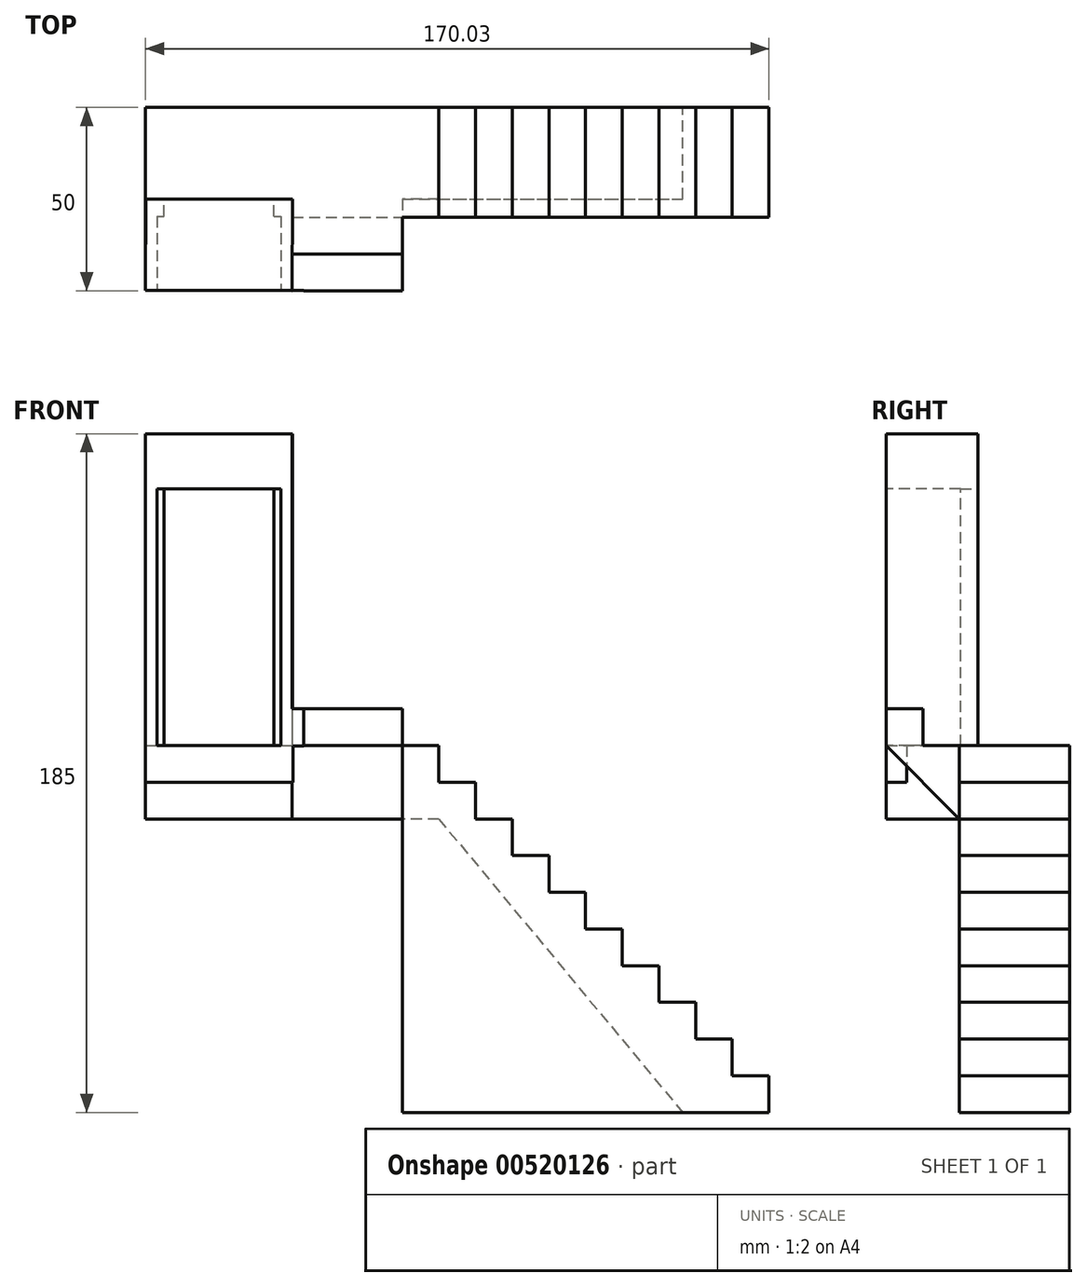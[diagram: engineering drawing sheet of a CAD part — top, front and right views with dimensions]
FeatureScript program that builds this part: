
annotation { "Feature Type Name" : "Feature", "Feature Type Description" : "" }
export const myFeature = defineFeature(function(context is Context, id is Id, definition is map)
    precondition{}
    {
        {
            var Q0;
            Q0=qCreatedBy(makeId("Top.planeOp"),FACE);
            var sketch = newSketch(context, id + "F0", { "sketchPlane" : qUnion([Q0])});
            skLineSegment(sketch, "E0.bottom", {"start": v(-73.69, 46.23) * mm, "end": v(106.31, 46.23) * mm});
            skLineSegment(sketch, "E0.top", {"start": v(-33.69, 16.23) * mm, "end": v(106.31, 16.23) * mm});
            skLineSegment(sketch, "E0.left", {"start": v(-73.69, 46.23) * mm, "end": v(-73.69, 16.23) * mm});
            skLineSegment(sketch, "E0.right", {"start": v(106.31, 46.23) * mm, "end": v(106.31, 16.23) * mm});
            skLineSegment(sketch, "E1", {"start": v(-3.69, 16.23) * mm, "end": v(-3.69, -3.77) * mm});
            skLineSegment(sketch, "E2", {"start": v(-3.69, -3.77) * mm, "end": v(-33.69, -3.77) * mm});
            skLineSegment(sketch, "E3", {"start": v(-33.69, -3.77) * mm, "end": v(-33.69, 16.23) * mm});
            skLineSegment(sketch, "E4", {"start": v(-33.69, 16.23) * mm, "end": v(-33.69, 46.23) * mm});
            skLineSegment(sketch, "E5", {"start": v(-73.69, 16.23) * mm, "end": v(-73.69, -3.71) * mm});
            skLineSegment(sketch, "E6", {"start": v(-73.69, -3.71) * mm, "end": v(-33.69, -3.77) * mm});
            skSolve(sketch);
        }
        {
            var Q0;
            Q0 = qSketchRegion(id + "F0", true);
            extrude(context, id + "F1", {"entities" : qUnion([Q0]), "depth" : 100 * mm, "offsetDistance" : 25 * mm});
        }
        {
            var Q0;
            Q0=makeQuery(id+"F1.opExtrude","SWEPT_FACE",FACE,{"disambiguationData":[OSD([sQuery(id+"F0.wireOp",EDGE,"E0.bottom")])]});
            var sketch = newSketch(context, id + "F2", { "sketchPlane" : qUnion([Q0])});
            skLineSegment(sketch, "E7", {"start": v(-6.31, 100) * mm, "end": v(-6.31, 0) * mm, "construction": true});
            skLineSegment(sketch, "E8", {"start": v(-106.31, 0) * mm, "end": v(-6.31, 100) * mm});
            skLineSegment(sketch, "E9", {"start": v(-6.31, 100) * mm, "end": v(-6.31, 80) * mm});
            skLineSegment(sketch, "E10", {"start": v(-6.31, 80) * mm, "end": v(73.69, 80) * mm});
            skLineSegment(sketch, "E11", {"start": v(-6.31, 80) * mm, "end": v(-6.31, 0) * mm});
            skSolve(sketch);
        }
        {
            var Q0;
            Q0 = qSketchRegion(id + "F2", true);
            var Q1;
            {var subQ0=sQuery(id+"F2.wireOp",EDGE,"E8");Q1=makeQuery(id+"F2.imprint","IMPRINT",FACE,{"disambiguationData":[TD([[makeQuery(id+"F2.imprint","IMPRINT",EDGE,{"derivedFrom":subQ0}),1.0]])]});}
            var Q2;
            {var subQ0=sQuery(id+"F2.wireOp",EDGE,"E10");Q2=makeQuery(id+"F2.imprint","IMPRINT",FACE,{"disambiguationData":[TD([[makeQuery(id+"F2.imprint","IMPRINT",EDGE,{"derivedFrom":subQ0}),-1.0]])]});}
            extrude(context, id + "F3", {"entities" : qUnion([Q0, Q1, Q2]), "operationType" : NewBodyOperationType.REMOVE, "oppositeDirection" : true, "depth" : 60 * mm, "offsetDistance" : 25 * mm});
        }
        {
            var Q0;
            Q0=makeQuery(id+"F1.opExtrude","SWEPT_FACE",FACE,{"disambiguationData":[OSD([sQuery(id+"F0.wireOp",EDGE,"E0.bottom")])]});
            var sketch = newSketch(context, id + "F4", { "sketchPlane" : qUnion([Q0])});
            skLineSegment(sketch, "E12.bottom", {"start": v(-6.31, 100) * mm, "end": v(-16.31, 100) * mm});
            skLineSegment(sketch, "E12.top", {"start": v(-6.31, 90) * mm, "end": v(-16.31, 90) * mm});
            skLineSegment(sketch, "E12.left", {"start": v(-6.31, 100) * mm, "end": v(-6.31, 90) * mm});
            skLineSegment(sketch, "E12.right", {"start": v(-16.31, 100) * mm, "end": v(-16.31, 90) * mm});
            skLineSegment(sketch, "E13.bottom", {"start": v(-16.31, 90) * mm, "end": v(-26.31, 90) * mm});
            skLineSegment(sketch, "E13.top", {"start": v(-16.31, 80) * mm, "end": v(-26.31, 80) * mm});
            skLineSegment(sketch, "E13.left", {"start": v(-16.31, 90) * mm, "end": v(-16.31, 80) * mm});
            skLineSegment(sketch, "E13.right", {"start": v(-26.31, 90) * mm, "end": v(-26.31, 80) * mm});
            skLineSegment(sketch, "E14.bottom", {"start": v(-26.31, 80) * mm, "end": v(-36.31, 80) * mm});
            skLineSegment(sketch, "E14.top", {"start": v(-26.31, 70) * mm, "end": v(-36.31, 70) * mm});
            skLineSegment(sketch, "E14.left", {"start": v(-26.31, 80) * mm, "end": v(-26.31, 70) * mm});
            skLineSegment(sketch, "E14.right", {"start": v(-36.31, 80) * mm, "end": v(-36.31, 70) * mm});
            skLineSegment(sketch, "E15.bottom", {"start": v(-36.31, 70) * mm, "end": v(-46.31, 70) * mm});
            skLineSegment(sketch, "E15.top", {"start": v(-36.31, 60) * mm, "end": v(-46.31, 60) * mm});
            skLineSegment(sketch, "E15.left", {"start": v(-36.31, 70) * mm, "end": v(-36.31, 60) * mm});
            skLineSegment(sketch, "E15.right", {"start": v(-46.31, 70) * mm, "end": v(-46.31, 60) * mm});
            skLineSegment(sketch, "E16.bottom", {"start": v(-46.31, 60) * mm, "end": v(-56.31, 60) * mm});
            skLineSegment(sketch, "E16.top", {"start": v(-46.31, 50) * mm, "end": v(-56.31, 50) * mm});
            skLineSegment(sketch, "E16.left", {"start": v(-46.31, 60) * mm, "end": v(-46.31, 50) * mm});
            skLineSegment(sketch, "E16.right", {"start": v(-56.31, 60) * mm, "end": v(-56.31, 50) * mm});
            skLineSegment(sketch, "E17.bottom", {"start": v(-56.31, 50) * mm, "end": v(-66.31, 50) * mm});
            skLineSegment(sketch, "E17.top", {"start": v(-56.31, 40) * mm, "end": v(-66.31, 40) * mm});
            skLineSegment(sketch, "E17.left", {"start": v(-56.31, 50) * mm, "end": v(-56.31, 40) * mm});
            skLineSegment(sketch, "E17.right", {"start": v(-66.31, 50) * mm, "end": v(-66.31, 40) * mm});
            skLineSegment(sketch, "E18.bottom", {"start": v(-66.31, 40) * mm, "end": v(-76.31, 40) * mm});
            skLineSegment(sketch, "E18.top", {"start": v(-66.31, 30) * mm, "end": v(-76.31, 30) * mm});
            skLineSegment(sketch, "E18.left", {"start": v(-66.31, 40) * mm, "end": v(-66.31, 30) * mm});
            skLineSegment(sketch, "E18.right", {"start": v(-76.31, 40) * mm, "end": v(-76.31, 30) * mm});
            skLineSegment(sketch, "E19.bottom", {"start": v(-76.31, 30) * mm, "end": v(-86.31, 30) * mm});
            skLineSegment(sketch, "E19.top", {"start": v(-76.31, 20) * mm, "end": v(-86.31, 20) * mm});
            skLineSegment(sketch, "E19.left", {"start": v(-76.31, 30) * mm, "end": v(-76.31, 20) * mm});
            skLineSegment(sketch, "E19.right", {"start": v(-86.31, 30) * mm, "end": v(-86.31, 20) * mm});
            skLineSegment(sketch, "E20.bottom", {"start": v(-86.31, 20) * mm, "end": v(-96.31, 20) * mm});
            skLineSegment(sketch, "E20.top", {"start": v(-86.31, 10) * mm, "end": v(-96.31, 10) * mm});
            skLineSegment(sketch, "E20.left", {"start": v(-86.31, 20) * mm, "end": v(-86.31, 10) * mm});
            skLineSegment(sketch, "E20.right", {"start": v(-96.31, 20) * mm, "end": v(-96.31, 10) * mm});
            skLineSegment(sketch, "E21.bottom", {"start": v(-96.31, 10) * mm, "end": v(-106.31, 10) * mm});
            skLineSegment(sketch, "E21.top", {"start": v(-96.31, 0) * mm, "end": v(-106.31, 0) * mm});
            skLineSegment(sketch, "E21.left", {"start": v(-96.31, 10) * mm, "end": v(-96.31, 0) * mm});
            skLineSegment(sketch, "E21.right", {"start": v(-106.31, 10) * mm, "end": v(-106.31, 0) * mm});
            skSolve(sketch);
        }
        {
            var Q0;
            Q0 = qSketchRegion(id + "F4", true);
            extrude(context, id + "F5", {"entities" : qUnion([Q0]), "operationType" : NewBodyOperationType.REMOVE, "oppositeDirection" : true, "depth" : 40 * mm, "offsetDistance" : 25 * mm});
        }
        {
            var Q0;
            Q0=makeQuery(id+"F5.boolean.opBoolean","MERGE",FACE,{"derivedFrom":[makeQuery(id+"F1.opExtrude","SWEPT_FACE",FACE,{"disambiguationData":[OSD([sQuery(id+"F0.wireOp",EDGE,"E1")])]}),makeQuery(id+"F5.opExtrude","SWEPT_FACE",FACE,{"disambiguationData":[OSD([sQuery(id+"F4.wireOp",EDGE,"E12.left")])]})]});
            var sketch = newSketch(context, id + "F6", { "sketchPlane" : qUnion([Q0])});
            skLineSegment(sketch, "E22", {"start": v(-3.77, 100) * mm, "end": v(16.23, 80) * mm});
            skSolve(sketch);
        }
        {
            var Q0;
            Q0 = qSketchRegion(id + "F6", true);
            var Q1;
            Q1=makeQuery(id+"F6.imprint","IMPRINT",FACE,{"disambiguationData":[TD([[makeQuery(id+"F6.imprint","IMPRINT",EDGE,{"derivedFrom":sQuery(id+"F6.wireOp",EDGE,"E22")}),-1.0]])]});
            extrude(context, id + "F7", {"entities" : qUnion([Q0, Q1]), "operationType" : NewBodyOperationType.REMOVE, "oppositeDirection" : true, "depth" : 30 * mm, "offsetDistance" : 25 * mm});
        }
        {
            var Q0;
            Q0=makeQuery(id+"F5.boolean.opBoolean","MERGE",FACE,{"derivedFrom":[makeQuery(id+"F1.opExtrude","SWEPT_FACE",FACE,{"disambiguationData":[OSD([sQuery(id+"F0.wireOp",EDGE,"E1")])]}),makeQuery(id+"F5.opExtrude","SWEPT_FACE",FACE,{"disambiguationData":[OSD([sQuery(id+"F4.wireOp",EDGE,"E12.left")])]})]});
            var sketch = newSketch(context, id + "F8", { "sketchPlane" : qUnion([Q0])});
            skLineSegment(sketch, "E23", {"start": v(-3.77, 100) * mm, "end": v(-3.77, 120) * mm});
            skLineSegment(sketch, "E24", {"start": v(-3.77, 120) * mm, "end": v(16.23, 100) * mm});
            skLineSegment(sketch, "E25", {"start": v(16.23, 100) * mm, "end": v(-3.77, 100) * mm});
            skSolve(sketch);
        }
        {
            var Q0;
            Q0 = qSketchRegion(id + "F8", true);
            extrude(context, id + "F9", {"entities" : qUnion([Q0]), "operationType" : NewBodyOperationType.ADD, "oppositeDirection" : true, "depth" : 30 * mm, "offsetDistance" : 25 * mm});
        }
        {
            var Q0;
            Q0=makeQuery(id+"F9.boolean.opBoolean","MERGE",FACE,{"derivedFrom":[makeQuery(id+"F5.boolean.opBoolean","MERGE",FACE,{"derivedFrom":[makeQuery(id+"F1.opExtrude","SWEPT_FACE",FACE,{"disambiguationData":[OSD([sQuery(id+"F0.wireOp",EDGE,"E1")])]}),makeQuery(id+"F5.opExtrude","SWEPT_FACE",FACE,{"disambiguationData":[OSD([sQuery(id+"F4.wireOp",EDGE,"E12.left")])]})]}),makeQuery(id+"F9.opExtrude","CAP_FACE",FACE,{"disambiguationData":[OSD([sQuery(id+"F8.wireOp",EDGE,"E23"),sQuery(id+"F8.wireOp",EDGE,"E24"),sQuery(id+"F8.wireOp",EDGE,"E25")])],"isStart":true})]});
            var sketch = newSketch(context, id + "F10", { "sketchPlane" : qUnion([Q0])});
            skLineSegment(sketch, "E26.bottom", {"start": v(-3.77, 120) * mm, "end": v(6.23, 120) * mm});
            skLineSegment(sketch, "E26.top", {"start": v(-3.77, 110) * mm, "end": v(6.23, 110) * mm});
            skLineSegment(sketch, "E26.left", {"start": v(-3.77, 120) * mm, "end": v(-3.77, 110) * mm});
            skLineSegment(sketch, "E26.right", {"start": v(6.23, 120) * mm, "end": v(6.23, 110) * mm});
            skLineSegment(sketch, "E27.bottom", {"start": v(6.23, 110) * mm, "end": v(16.23, 110) * mm});
            skLineSegment(sketch, "E27.top", {"start": v(6.23, 100) * mm, "end": v(16.23, 100) * mm});
            skLineSegment(sketch, "E27.left", {"start": v(6.23, 110) * mm, "end": v(6.23, 100) * mm});
            skLineSegment(sketch, "E27.right", {"start": v(16.23, 110) * mm, "end": v(16.23, 100) * mm});
            skSolve(sketch);
        }
        {
            var Q0;
            Q0 = qSketchRegion(id + "F10", true);
            extrude(context, id + "F11", {"entities" : qUnion([Q0]), "operationType" : NewBodyOperationType.REMOVE, "oppositeDirection" : true, "depth" : 30 * mm, "offsetDistance" : 25 * mm});
        }
        {
            var Q0;
            Q0=makeQuery(id+"F1.opExtrude","SWEPT_FACE",FACE,{"disambiguationData":[OSD([sQuery(id+"F0.wireOp",EDGE,"E6")])]});
            var sketch = newSketch(context, id + "F12", { "sketchPlane" : qUnion([Q0])});
            skLineSegment(sketch, "E28.bottom", {"start": v(-33.68, 100) * mm, "end": v(-73.68, 100) * mm});
            skLineSegment(sketch, "E28.top", {"start": v(-33.68, 185) * mm, "end": v(-73.68, 185) * mm});
            skLineSegment(sketch, "E28.left", {"start": v(-33.68, 100) * mm, "end": v(-33.68, 185) * mm});
            skLineSegment(sketch, "E28.right", {"start": v(-73.68, 100) * mm, "end": v(-73.68, 185) * mm});
            skSolve(sketch);
        }
        {
            var Q0;
            Q0 = qSketchRegion(id + "F12", true);
            extrude(context, id + "F13", {"entities" : qUnion([Q0]), "operationType" : NewBodyOperationType.ADD, "endBound" : BoundingType.SYMMETRIC, "depth" : 50 * mm, "offsetDistance" : 25 * mm});
        }
        {
            var Q0;
            Q0=makeQuery(id+"F13.opExtrude","CAP_FACE",FACE,{"disambiguationData":[OSD([sQuery(id+"F12.wireOp",EDGE,"E28.bottom"),sQuery(id+"F12.wireOp",EDGE,"E28.top"),sQuery(id+"F12.wireOp",EDGE,"E28.left"),sQuery(id+"F12.wireOp",EDGE,"E28.right")])],"isStart":true});
            var sketch = newSketch(context, id + "F14", { "sketchPlane" : qUnion([Q0])});
            skLineSegment(sketch, "E29.bottom", {"start": v(38.68, 100) * mm, "end": v(68.68, 100) * mm});
            skLineSegment(sketch, "E29.top", {"start": v(38.68, 170) * mm, "end": v(68.68, 170) * mm});
            skLineSegment(sketch, "E29.left", {"start": v(38.68, 100) * mm, "end": v(38.68, 170) * mm});
            skLineSegment(sketch, "E29.right", {"start": v(68.68, 100) * mm, "end": v(68.68, 170) * mm});
            skSolve(sketch);
        }
        {
            var Q0;
            Q0=makeQuery(id+"F13.opExtrude","SWEPT_FACE",FACE,{"disambiguationData":[OSD([sQuery(id+"F12.wireOp",EDGE,"E28.top")])]});
            var sketch = newSketch(context, id + "F15", { "sketchPlane" : qUnion([Q0])});
            skLineSegment(sketch, "E30.bottom", {"start": v(-70.56, 16.52) * mm, "end": v(-36.8, 16.52) * mm});
            skLineSegment(sketch, "E30.top", {"start": v(-70.56, -25.45) * mm, "end": v(-36.8, -25.45) * mm});
            skLineSegment(sketch, "E30.left", {"start": v(-70.56, 16.52) * mm, "end": v(-70.56, -25.45) * mm});
            skLineSegment(sketch, "E30.right", {"start": v(-36.8, 16.52) * mm, "end": v(-36.8, -25.45) * mm});
            skSolve(sketch);
        }
        {
            var Q0;
            Q0 = qSketchRegion(id + "F15", true);
            extrude(context, id + "F16", {"entities" : qUnion([Q0]), "operationType" : NewBodyOperationType.REMOVE, "oppositeDirection" : true, "depth" : 85 * mm, "offsetDistance" : 25 * mm});
        }
        {
            var Q0;
            Q0 = qSketchRegion(id + "F14", true);
            extrude(context, id + "F17", {"entities" : qUnion([Q0]), "operationType" : NewBodyOperationType.REMOVE, "oppositeDirection" : true, "depth" : 10 * mm, "offsetDistance" : 25 * mm});
        }
        {
            var Q0;
            Q0=makeQuery(id+"F13.opExtrude","SWEPT_FACE",FACE,{"disambiguationData":[OSD([sQuery(id+"F12.wireOp",EDGE,"E28.top")])]});
            var sketch = newSketch(context, id + "F18", { "sketchPlane" : qUnion([Q0])});
            skLineSegment(sketch, "E31.bottom", {"start": v(-70.56, 16.52) * mm, "end": v(-36.8, 16.52) * mm});
            skLineSegment(sketch, "E31.top", {"start": v(-70.56, -25.45) * mm, "end": v(-36.8, -25.45) * mm});
            skLineSegment(sketch, "E31.left", {"start": v(-70.56, 16.52) * mm, "end": v(-70.56, -25.45) * mm});
            skLineSegment(sketch, "E31.right", {"start": v(-36.8, 16.52) * mm, "end": v(-36.8, -25.45) * mm});
            skSolve(sketch);
        }
        {
            var Q0;
            Q0 = qSketchRegion(id + "F18", true);
            extrude(context, id + "F19", {"entities" : qUnion([Q0]), "operationType" : NewBodyOperationType.ADD, "oppositeDirection" : true, "depth" : 15 * mm, "offsetDistance" : 25 * mm});
        }
        {
            var Q0;
            Q0=makeQuery(id+"F13.opExtrude","SWEPT_FACE",FACE,{"disambiguationData":[OSD([sQuery(id+"F12.wireOp",EDGE,"E28.bottom")])]});
            var sketch = newSketch(context, id + "F20", { "sketchPlane" : qUnion([Q0])});
            skLineSegment(sketch, "E32.bottom", {"start": v(-73.72, 28.71) * mm, "end": v(-33.42, 28.71) * mm});
            skLineSegment(sketch, "E32.top", {"start": v(-73.72, -1.8) * mm, "end": v(-33.42, -1.8) * mm});
            skLineSegment(sketch, "E32.left", {"start": v(-73.72, 28.71) * mm, "end": v(-73.72, -1.8) * mm});
            skLineSegment(sketch, "E32.right", {"start": v(-33.42, 28.71) * mm, "end": v(-33.42, -1.8) * mm});
            skSolve(sketch);
        }
        {
            var Q0;
            Q0 = qSketchRegion(id + "F20", true);
            extrude(context, id + "F21", {"entities" : qUnion([Q0]), "operationType" : NewBodyOperationType.ADD, "depth" : 10 * mm, "offsetDistance" : 25 * mm});
        }
        {
            var Q0;
            Q0=makeQuery(id+"F21.opExtrude","CAP_FACE",FACE,{"disambiguationData":[OSD([sQuery(id+"F20.wireOp",EDGE,"E32.bottom"),sQuery(id+"F20.wireOp",EDGE,"E32.top"),sQuery(id+"F20.wireOp",EDGE,"E32.left"),sQuery(id+"F20.wireOp",EDGE,"E32.right")])],"isStart":false});
            var sketch = newSketch(context, id + "F22", { "sketchPlane" : qUnion([Q0])});
            skLineSegment(sketch, "E33.bottom", {"start": v(-77.8, 3.71) * mm, "end": v(-30.52, 3.71) * mm});
            skLineSegment(sketch, "E33.top", {"start": v(-77.8, 33.4) * mm, "end": v(-30.52, 33.4) * mm});
            skLineSegment(sketch, "E33.left", {"start": v(-77.8, 3.71) * mm, "end": v(-77.8, 33.4) * mm});
            skLineSegment(sketch, "E33.right", {"start": v(-30.52, 3.71) * mm, "end": v(-30.52, 33.4) * mm});
            skSolve(sketch);
        }
        {
            var Q0;
            Q0 = qSketchRegion(id + "F22", true);
            extrude(context, id + "F23", {"entities" : qUnion([Q0]), "operationType" : NewBodyOperationType.REMOVE, "oppositeDirection" : true, "depth" : 100 * mm, "offsetDistance" : 25 * mm});
        }
        {
            var Q0;
            Q0=makeQuery(id+"F1.opExtrude","SWEPT_FACE",FACE,{"disambiguationData":[OSD([sQuery(id+"F0.wireOp",EDGE,"E0.bottom")])]});
            var sketch = newSketch(context, id + "F24", { "sketchPlane" : qUnion([Q0])});
            skLineSegment(sketch, "E34", {"start": v(-6.31, 0) * mm, "end": v(-6.31, 80) * mm});
            skLineSegment(sketch, "E35", {"start": v(-6.31, 80) * mm, "end": v(-72.8, 0) * mm});
            skLineSegment(sketch, "E36", {"start": v(-72.8, 0) * mm, "end": v(-6.31, 0) * mm});
            skSolve(sketch);
        }
        {
            var Q0;
            Q0=makeQuery(id+"F24.imprint","IMPRINT",FACE,{"disambiguationData":[TD([[makeQuery(id+"F24.imprint","IMPRINT",EDGE,{"derivedFrom":sQuery(id+"F24.wireOp",EDGE,"E34")}),-1.0]])]});
            extrude(context, id + "F25", {"entities" : qUnion([Q0]), "operationType" : NewBodyOperationType.REMOVE, "oppositeDirection" : true, "depth" : 30 * mm, "offsetDistance" : 25 * mm});
        }
        {
            var Q0;
            Q0=makeQuery(id+"F1.opExtrude","SWEPT_FACE",FACE,{"disambiguationData":[OSD([sQuery(id+"F0.wireOp",EDGE,"E0.top")])]});
            var sketch = newSketch(context, id + "F26", { "sketchPlane" : qUnion([Q0])});
            skLineSegment(sketch, "E37", {"start": v(-3.69, 0) * mm, "end": v(72.8, 0) * mm});
            skLineSegment(sketch, "E38", {"start": v(72.8, 0) * mm, "end": v(6.31, 80) * mm});
            skLineSegment(sketch, "E39", {"start": v(-3.69, 80) * mm, "end": v(-3.69, 0) * mm});
            skPoint(sketch, "E40.orphan", {"position": v(-7.27, 0) * mm});
            skLineSegment(sketch, "E41", {"start": v(-3.69, 80) * mm, "end": v(6.31, 80) * mm});
            skSolve(sketch);
        }
        {
            var Q0;
            Q0 = qSketchRegion(id + "F26", true);
            extrude(context, id + "F27", {"entities" : qUnion([Q0]), "operationType" : NewBodyOperationType.ADD, "oppositeDirection" : true, "depth" : 5 * mm, "offsetDistance" : 25 * mm});
        }
    });
